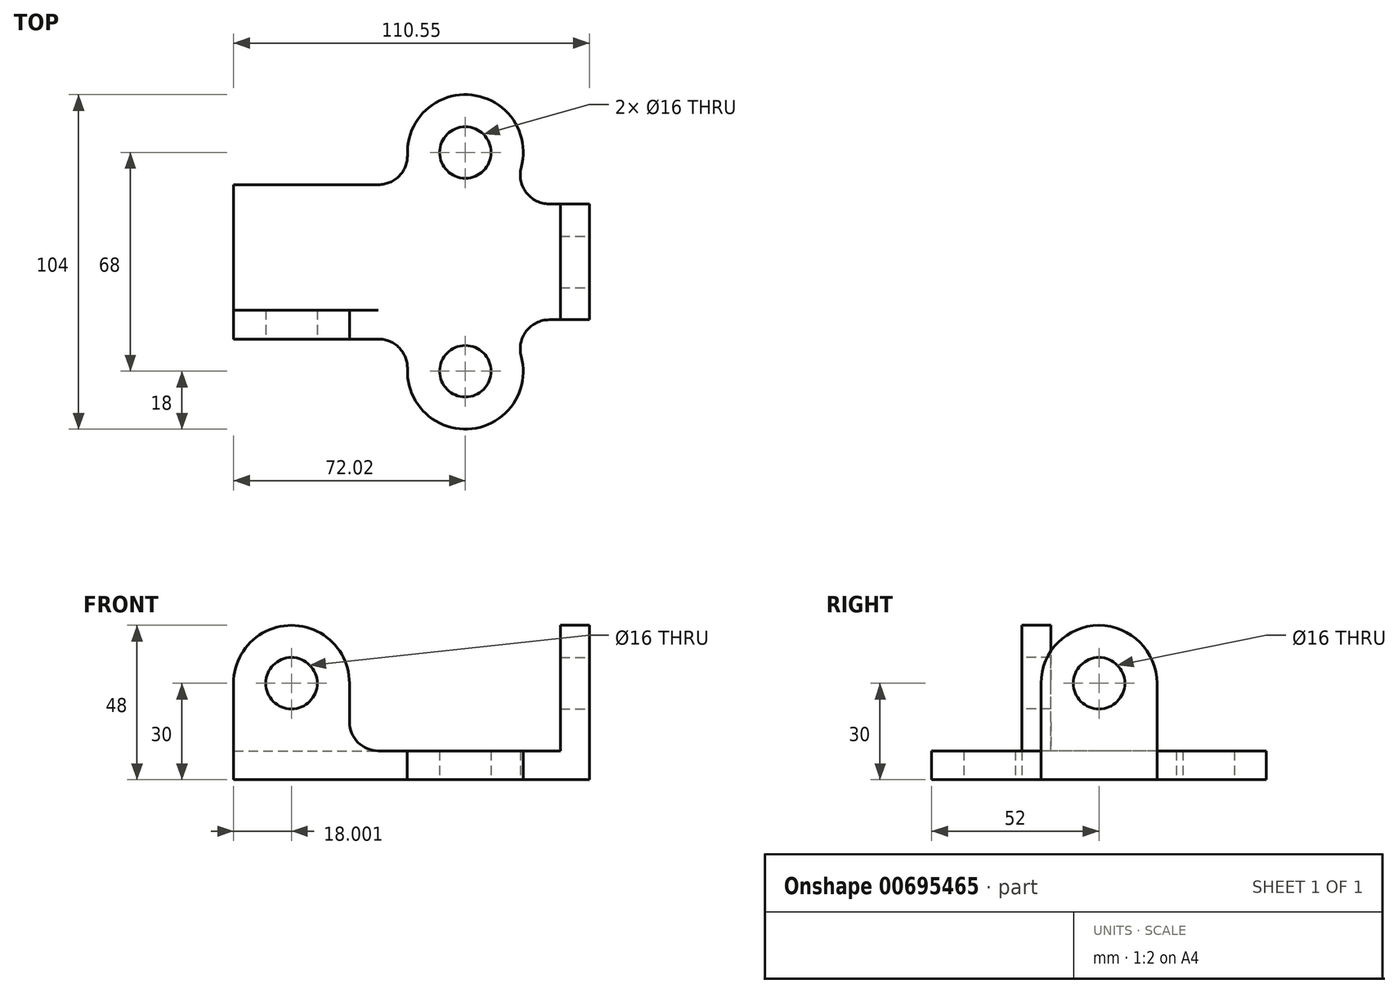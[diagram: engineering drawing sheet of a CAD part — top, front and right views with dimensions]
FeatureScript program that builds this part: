
annotation { "Feature Type Name" : "Feature", "Feature Type Description" : "" }
export const myFeature = defineFeature(function(context is Context, id is Id, definition is map)
    precondition{}
    {
        {
            var Q0;
            Q0=qCreatedBy(makeId("Top.planeOp"),FACE);
            var sketch = newSketch(context, id + "F0", { "sketchPlane" : qUnion([Q0])});
            skCircle(sketch, "E0", {"center": v(0, 34) * mm, "radius": 8 * mm});
            skCircle(sketch, "E1", {"center": v(0, -34) * mm, "radius": 8 * mm});
            skArc(sketch, "E2", {"start": v(17.99, 33.33) * mm, "mid": v(0, 52) * mm, "end": v(-17.99, 33.33) * mm});
            skArc(sketch, "E3", {"start": v(-17.99, -33.33) * mm, "mid": v(0, -52) * mm, "end": v(17.99, -33.33) * mm});
            skLineSegment(sketch, "E4", {"start": v(-72, 24) * mm, "end": v(-26.98, 24) * mm});
            skLineSegment(sketch, "E5", {"start": v(-72, -24) * mm, "end": v(-26.98, -24) * mm});
            skArc(sketch, "E6", {"start": v(-26.98, 24) * mm, "mid": v(-20.5, 26.76) * mm, "end": v(-17.99, 33.33) * mm});
            skArc(sketch, "E7", {"start": v(-17.99, -33.33) * mm, "mid": v(-20.5, -26.76) * mm, "end": v(-26.98, -24) * mm});
            skLineSegment(sketch, "E8", {"start": v(-72, 24) * mm, "end": v(-72, -24) * mm});
            skArc(sketch, "E9", {"start": v(17.38, 29.33) * mm, "mid": v(2.02, 51.89) * mm, "end": v(-17.99, 33.33) * mm});
            skArc(sketch, "E10", {"start": v(-17.99, -33.33) * mm, "mid": v(2.02, -51.89) * mm, "end": v(17.38, -29.33) * mm});
            skArc(sketch, "E11", {"start": v(26.08, -18) * mm, "mid": v(18.94, -21.52) * mm, "end": v(17.38, -29.33) * mm});
            skArc(sketch, "E12", {"start": v(17.38, 29.33) * mm, "mid": v(18.94, 21.52) * mm, "end": v(26.08, 18) * mm});
            skLineSegment(sketch, "E13", {"start": v(38.53, 18) * mm, "end": v(38.53, -18) * mm});
            skLineSegment(sketch, "E14", {"start": v(38.53, 18) * mm, "end": v(26.08, 18) * mm});
            skLineSegment(sketch, "E15", {"start": v(38.53, -18) * mm, "end": v(26.08, -18) * mm});
            skPoint(sketch, "E16.center.orphan", {"position": v(38.53, 0) * mm});
            skSolve(sketch);
        }
        {
            var Q0;
            Q0=makeQuery(id+"F0.imprint","IMPRINT",FACE,{"disambiguationData":[TD([[makeQuery(id+"F0.imprint","IMPRINT",EDGE,{"derivedFrom":sQuery(id+"F0.wireOp",EDGE,"E0")}),-1.0]])]});
            extrude(context, id + "F1", {"entities" : qUnion([Q0]), "depth" : 9 * mm, "offsetDistance" : 25 * mm});
        }
        {
            var Q0;
            Q0=makeQuery(id+"F1.opExtrude","SWEPT_FACE",FACE,{"disambiguationData":[OSD([sQuery(id+"F0.wireOp",EDGE,"E5")])]});
            var sketch = newSketch(context, id + "F2", { "sketchPlane" : qUnion([Q0])});
            skArc(sketch, "E17", {"start": v(-36.02, 30) * mm, "mid": v(-54.03, 48) * mm, "end": v(-72.02, 29.98) * mm});
            skArc(sketch, "E18", {"start": v(-36.02, 18) * mm, "mid": v(-33.38, 11.64) * mm, "end": v(-27.02, 9) * mm});
            skLineSegment(sketch, "E19", {"start": v(-72, 9) * mm, "end": v(-72.02, 29.98) * mm});
            skLineSegment(sketch, "E20", {"start": v(-36.02, 18) * mm, "end": v(-36.02, 30) * mm});
            skLineSegment(sketch, "E21", {"start": v(-72, 9) * mm, "end": v(-15.26, 9) * mm});
            skSolve(sketch);
        }
        {
            var Q0;
            Q0=makeQuery(id+"F2.imprint","IMPRINT",FACE,{"disambiguationData":[TD([[makeQuery(id+"F2.imprint","IMPRINT",EDGE,{"derivedFrom":sQuery(id+"F2.wireOp",EDGE,"E17")}),1.0]])]});
            extrude(context, id + "F3", {"entities" : qUnion([Q0]), "operationType" : NewBodyOperationType.ADD, "oppositeDirection" : true, "depth" : 9 * mm, "offsetDistance" : 25 * mm});
        }
        {
            var Q0;
            Q0=makeQuery(id+"F3.boolean.opBoolean","MERGE",FACE,{"derivedFrom":[makeQuery(id+"F1.opExtrude","SWEPT_FACE",FACE,{"disambiguationData":[OSD([sQuery(id+"F0.wireOp",EDGE,"E5")])]}),makeQuery(id+"F3.opExtrude","CAP_FACE",FACE,{"disambiguationData":[OSD([sQuery(id+"F2.wireOp",EDGE,"E17"),sQuery(id+"F2.wireOp",EDGE,"E18"),sQuery(id+"F2.wireOp",EDGE,"E19"),sQuery(id+"F2.wireOp",EDGE,"E20"),sQuery(id+"F2.wireOp",EDGE,"E21")])],"isStart":true})]});
            var sketch = newSketch(context, id + "F4", { "sketchPlane" : qUnion([Q0])});
            skCircle(sketch, "E22", {"center": v(-54.02, 30) * mm, "radius": 8 * mm});
            skSolve(sketch);
        }
        {
            var Q0;
            Q0=makeQuery(id+"F4.imprint","IMPRINT",FACE,{"disambiguationData":[TD([[makeQuery(id+"F4.imprint","IMPRINT",EDGE,{"derivedFrom":sQuery(id+"F4.wireOp",EDGE,"E22")}),1.0]])]});
            var Q1;
            Q1=makeQuery(id+"F3.opExtrude","CAP_FACE",FACE,{"disambiguationData":[OSD([sQuery(id+"F2.wireOp",EDGE,"E17"),sQuery(id+"F2.wireOp",EDGE,"E18"),sQuery(id+"F2.wireOp",EDGE,"E19"),sQuery(id+"F2.wireOp",EDGE,"E20"),sQuery(id+"F2.wireOp",EDGE,"E21")])],"isStart":false});
            extrude(context, id + "F5", {"entities" : qUnion([Q0]), "operationType" : NewBodyOperationType.REMOVE, "endBound" : BoundingType.UP_TO_SURFACE, "oppositeDirection" : true, "depth" : 25 * mm, "endBoundEntityFace" : qUnion([Q1]), "offsetDistance" : 25 * mm});
        }
        {
            var Q0;
            Q0=makeQuery(id+"F1.opExtrude","SWEPT_FACE",FACE,{"disambiguationData":[OSD([sQuery(id+"F0.wireOp",EDGE,"E13")])]});
            var sketch = newSketch(context, id + "F6", { "sketchPlane" : qUnion([Q0])});
            skArc(sketch, "E23", {"start": v(18, 30) * mm, "mid": v(0, 48) * mm, "end": v(-18, 30) * mm});
            skLineSegment(sketch, "E24", {"start": v(-18, 30) * mm, "end": v(-18, 0) * mm});
            skLineSegment(sketch, "E25", {"start": v(-18, 30) * mm, "end": v(18, 30) * mm, "construction": true});
            skLineSegment(sketch, "E26", {"start": v(18, 30) * mm, "end": v(18, 0) * mm});
            skSolve(sketch);
        }
        {
            var Q0;
            {var subQ0=sQuery(id+"F6.wireOp",EDGE,"E23");Q0=makeQuery(id+"F6.imprint","IMPRINT",FACE,{"disambiguationData":[TD([[makeQuery(id+"F6.imprint","IMPRINT",EDGE,{"derivedFrom":subQ0}),1.0]])]});}
            extrude(context, id + "F7", {"entities" : qUnion([Q0]), "operationType" : NewBodyOperationType.ADD, "oppositeDirection" : true, "depth" : 9 * mm, "offsetDistance" : 25 * mm});
        }
        {
            var Q0;
            {var subQ0=sQuery(id+"F0.wireOp",EDGE,"E13");Q0=makeQuery(id+"F7.boolean.opBoolean","MERGE",FACE,{"derivedFrom":[makeQuery(id+"F1.opExtrude","SWEPT_FACE",FACE,{"disambiguationData":[OSD([subQ0])]}),makeQuery(id+"F7.opExtrude","CAP_FACE",FACE,{"disambiguationData":[OSD([subQ0,sQuery(id+"F6.wireOp",EDGE,"E23"),sQuery(id+"F6.wireOp",EDGE,"E24"),sQuery(id+"F6.wireOp",EDGE,"E26")])],"isStart":true})]});}
            var sketch = newSketch(context, id + "F8", { "sketchPlane" : qUnion([Q0])});
            skCircle(sketch, "E27", {"center": v(0, 30) * mm, "radius": 8 * mm});
            skSolve(sketch);
        }
        {
            var Q0;
            Q0=makeQuery(id+"F8.imprint","IMPRINT",FACE,{"disambiguationData":[TD([[makeQuery(id+"F8.imprint","IMPRINT",EDGE,{"derivedFrom":sQuery(id+"F8.wireOp",EDGE,"E27")}),1.0]])]});
            extrude(context, id + "F9", {"entities" : qUnion([Q0]), "operationType" : NewBodyOperationType.REMOVE, "endBound" : BoundingType.UP_TO_NEXT, "oppositeDirection" : true, "depth" : 25 * mm, "offsetDistance" : 25 * mm});
        }
    });
